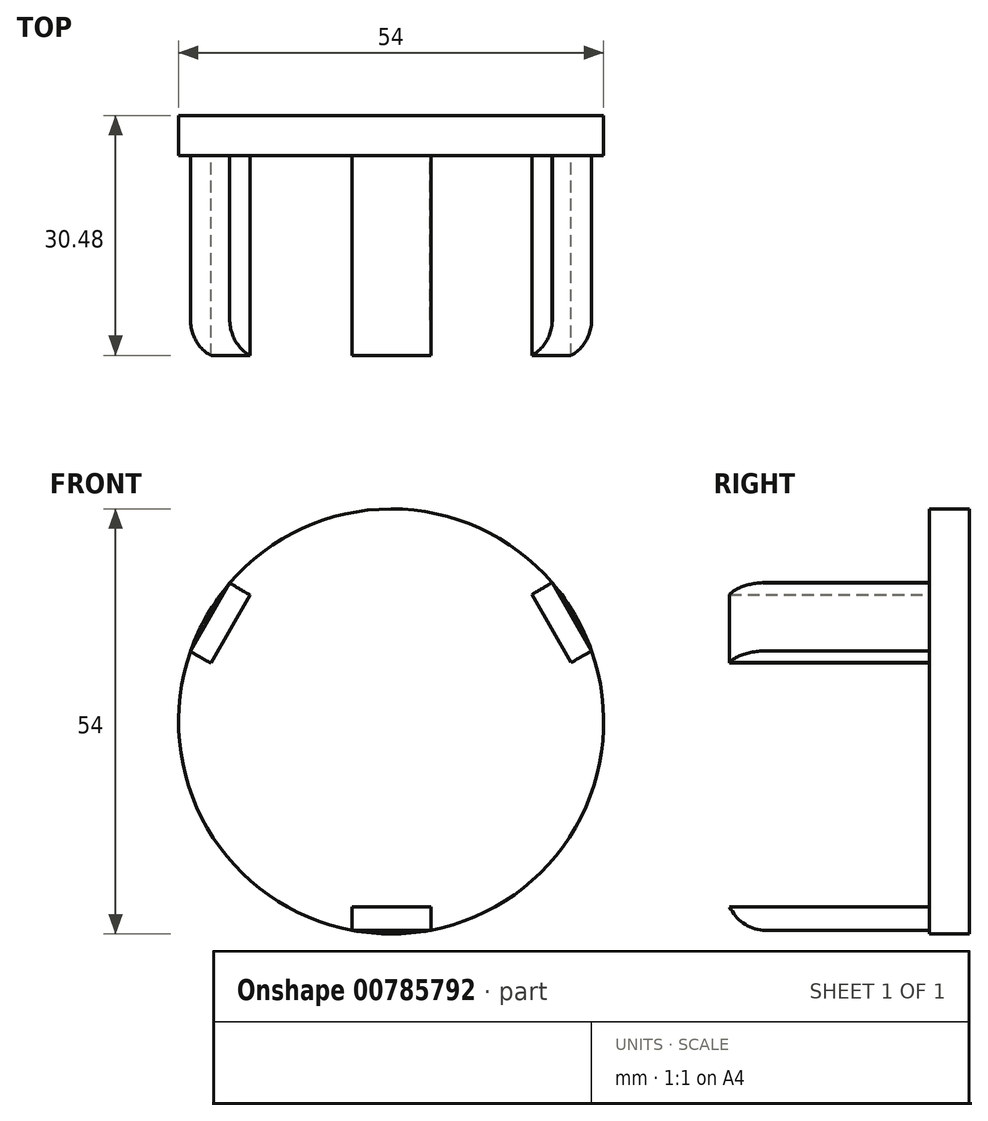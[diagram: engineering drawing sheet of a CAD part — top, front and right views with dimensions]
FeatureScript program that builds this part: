
annotation { "Feature Type Name" : "Feature", "Feature Type Description" : "" }
export const myFeature = defineFeature(function(context is Context, id is Id, definition is map)
    precondition{}
    {
        {
            var Q0;
            Q0=qCreatedBy(makeId("Front.planeOp"),FACE);
            var sketch = newSketch(context, id + "F0", { "sketchPlane" : qUnion([Q0])});
            skCircle(sketch, "E0", {"center": v(0, 0) * mm, "radius": 27 * mm});
            skSolve(sketch);
        }
        {
            var Q0;
            Q0=makeQuery(id+"F0.imprint","IMPRINT",FACE,{"disambiguationData":[TD([[makeQuery(id+"F0.imprint","IMPRINT",EDGE,{"derivedFrom":sQuery(id+"F0.wireOp",EDGE,"E0")}),1.0]])]});
            extrude(context, id + "F1", {"entities" : qUnion([Q0]), "depth" : 5.08 * mm, "offsetDistance" : 25.4 * mm});
        }
        {
            var Q0;
            Q0=makeQuery(id+"F1.opExtrude","CAP_FACE",FACE,{"disambiguationData":[OSD([sQuery(id+"F0.wireOp",EDGE,"E0")])],"isStart":false});
            var sketch = newSketch(context, id + "F2", { "sketchPlane" : qUnion([Q0])});
            skLineSegment(sketch, "E1.bottom", {"start": v(-4.96, -26.54) * mm, "end": v(5.04, -26.54) * mm});
            skLineSegment(sketch, "E1.top", {"start": v(-4.96, -23.54) * mm, "end": v(5.04, -23.54) * mm});
            skLineSegment(sketch, "E1.left", {"start": v(-4.96, -26.54) * mm, "end": v(-4.96, -23.54) * mm});
            skLineSegment(sketch, "E1.right", {"start": v(5.04, -26.54) * mm, "end": v(5.04, -23.54) * mm});
            skLineSegment(sketch, "E2.1.0", {"start": v(20.46, 17.64) * mm, "end": v(17.87, 16.14) * mm});
            skLineSegment(sketch, "E2.1.1", {"start": v(25.46, 8.98) * mm, "end": v(22.87, 7.48) * mm});
            skLineSegment(sketch, "E2.1.2", {"start": v(22.87, 7.48) * mm, "end": v(17.87, 16.14) * mm});
            skLineSegment(sketch, "E2.1.3", {"start": v(25.46, 8.98) * mm, "end": v(20.46, 17.64) * mm});
            skLineSegment(sketch, "E2.2.0", {"start": v(-25.5, 8.9) * mm, "end": v(-22.9, 7.4) * mm});
            skLineSegment(sketch, "E2.2.1", {"start": v(-20.5, 17.56) * mm, "end": v(-17.9, 16.06) * mm});
            skLineSegment(sketch, "E2.2.2", {"start": v(-17.9, 16.06) * mm, "end": v(-22.9, 7.4) * mm});
            skLineSegment(sketch, "E2.2.3", {"start": v(-20.5, 17.56) * mm, "end": v(-25.5, 8.9) * mm});
            skPoint(sketch, "E2.center", {"position": v(0, 0) * mm});
            skSolve(sketch);
        }
        {
            var Q0;
            {var subQ1=sQuery(id+"F2.wireOp",EDGE,"E2.2.1");Q0=makeQuery(id+"F2.imprint","IMPRINT",FACE,{"disambiguationData":[TD([[makeQuery(id+"F2.imprint","IMPRINT",EDGE,{"derivedFrom":subQ1}),-1.0]])]});}
            var Q1;
            {var subQ1=sQuery(id+"F2.wireOp",EDGE,"E2.1.1");Q1=makeQuery(id+"F2.imprint","IMPRINT",FACE,{"disambiguationData":[TD([[makeQuery(id+"F2.imprint","IMPRINT",EDGE,{"derivedFrom":subQ1}),-1.0]])]});}
            var Q2;
            {var subQ1=sQuery(id+"F2.wireOp",EDGE,"E1.top");Q2=makeQuery(id+"F2.imprint","IMPRINT",FACE,{"disambiguationData":[TD([[makeQuery(id+"F2.imprint","IMPRINT",EDGE,{"derivedFrom":subQ1}),-1.0]])]});}
            extrude(context, id + "F3", {"entities" : qUnion([Q0, Q1, Q2]), "operationType" : NewBodyOperationType.ADD, "depth" : 25.4 * mm, "offsetDistance" : 25.4 * mm});
        }
        {
            var Q0;
            Q0=makeQuery(id+"F3.opExtrude","CAP_EDGE",EDGE,{"disambiguationData":[OSD([sQuery(id+"F2.wireOp",EDGE,"E2.2.3")])],"isStart":false});
            var Q1;
            Q1=makeQuery(id+"F3.opExtrude","CAP_EDGE",EDGE,{"disambiguationData":[OSD([sQuery(id+"F2.wireOp",EDGE,"E1.bottom")])],"isStart":false});
            var Q2;
            Q2=makeQuery(id+"F3.opExtrude","CAP_EDGE",EDGE,{"disambiguationData":[OSD([sQuery(id+"F2.wireOp",EDGE,"E2.1.3")])],"isStart":false});
            fillet(context, id + "F4", {"entities" : qUnion([Q0, Q1, Q2]), "radius" : 5.08 * mm, "tangentPropagation" : true, "allowEdgeOverflow" : false});
        }
    });
